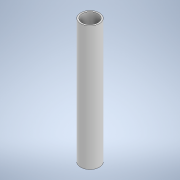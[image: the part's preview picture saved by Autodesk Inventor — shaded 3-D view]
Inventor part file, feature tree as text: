
AUTODESK INVENTOR PART (.ipt)
format: ipt  version: 2022 (Build 260153000, 153)  size: 96,768 bytes
history: native  units: mm
features: other x1, extrude x1, sketch x1
ambient origin geometry x8: Origin, YZ Plane, XZ Plane, XY Plane, X Axis, Y Axis, Z Axis, Center Point
bodies: Body1 (feature_tree)
feature tree (3):
  other  "Sólido1"
  extrude  "Extrusión1"  Depth=141.29mm
  sketch  "Boceto1"  dims[d0=21.36mm d1=17.92mm d2=141.29mm d3=0.0mm]
